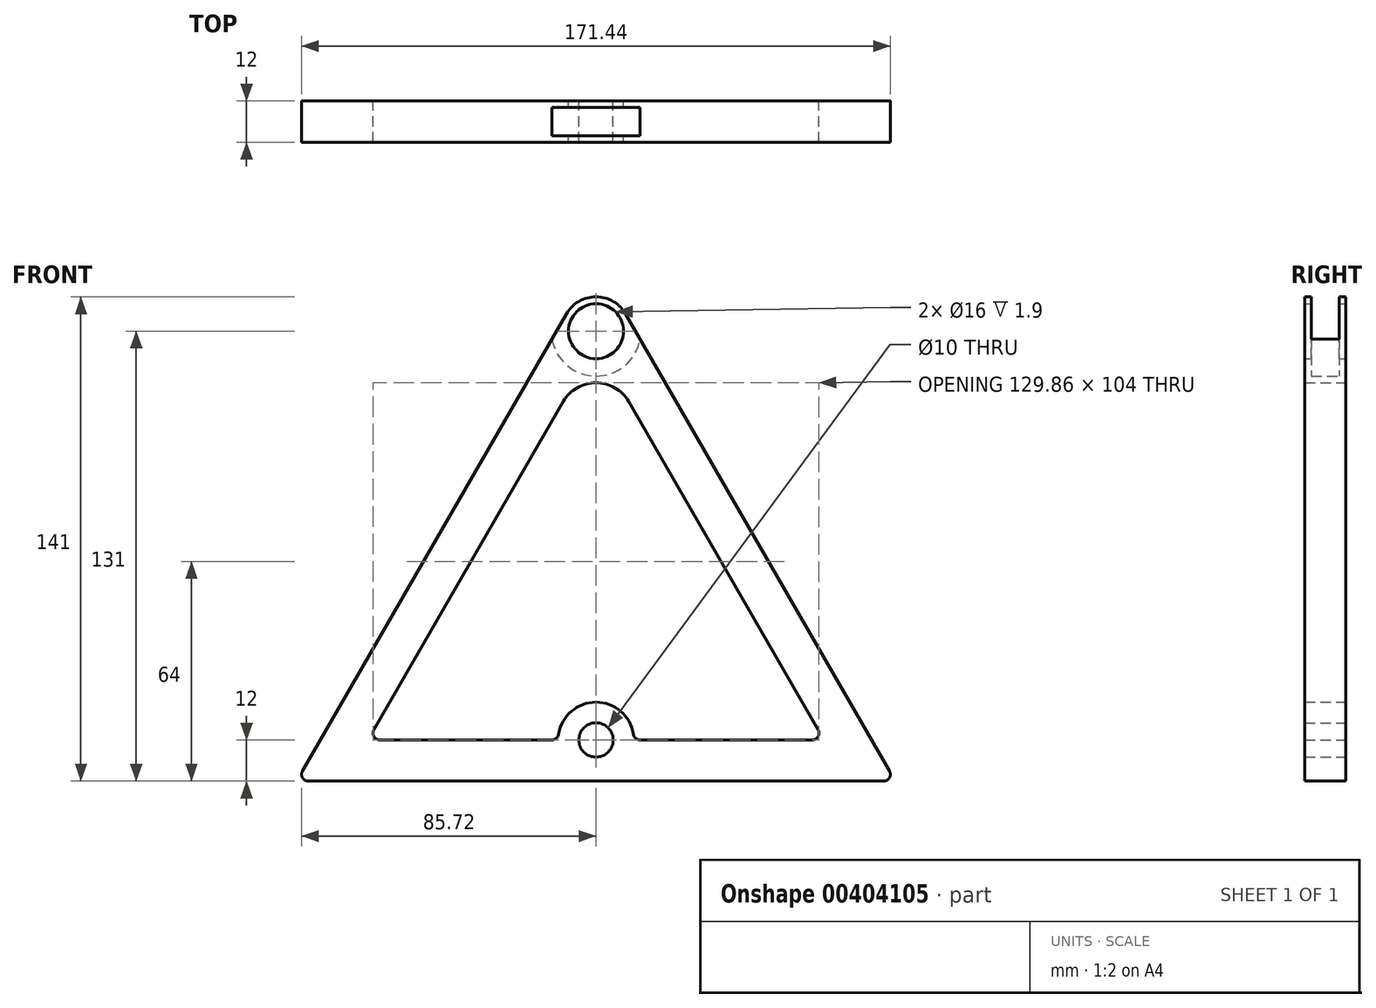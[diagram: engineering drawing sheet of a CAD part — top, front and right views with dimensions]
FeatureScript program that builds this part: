
annotation { "Feature Type Name" : "Feature", "Feature Type Description" : "" }
export const myFeature = defineFeature(function(context is Context, id is Id, definition is map)
    precondition{}
    {
        {
            var Q0;
            Q0=qCreatedBy(makeId("Front.planeOp"),FACE);
            var sketch = newSketch(context, id + "F0", { "sketchPlane" : qUnion([Q0])});
            skCircle(sketch, "E0", {"center": v(0, 125) * mm, "radius": 8 * mm, "construction": true});
            skCircle(sketch, "E1", {"center": v(0, 125) * mm, "radius": 5 * mm, "construction": true});
            skLineSegment(sketch, "E2", {"start": v(-72.17, 0) * mm, "end": v(72.17, 0) * mm, "construction": true});
            skLineSegment(sketch, "E3", {"start": v(72.17, 0) * mm, "end": v(0, 125) * mm, "construction": true});
            skLineSegment(sketch, "E4", {"start": v(0, 125) * mm, "end": v(-72.17, 0) * mm, "construction": true});
            skSolve(sketch);
        }
        {
            var Q0;
            Q0=qCreatedBy(makeId("Front.planeOp"),FACE);
            var sketch = newSketch(context, id + "F1", { "sketchPlane" : qUnion([Q0])});
            skLineSegment(sketch, "E5", {"start": v(-83.72, -6) * mm, "end": v(83.72, -6) * mm});
            skLineSegment(sketch, "E6", {"start": v(85.45, -3) * mm, "end": v(8.66, 130) * mm});
            skLineSegment(sketch, "E7", {"start": v(-85.45, -3) * mm, "end": v(-8.66, 130) * mm});
            skLineSegment(sketch, "E8", {"start": v(-62.93, 6) * mm, "end": v(-12.85, 6) * mm});
            skLineSegment(sketch, "E9", {"start": v(64.66, 9) * mm, "end": v(9.53, 104.5) * mm});
            skLineSegment(sketch, "E10", {"start": v(-64.66, 9) * mm, "end": v(-9.53, 104.5) * mm});
            skCircle(sketch, "E11", {"center": v(0, 6) * mm, "radius": 5 * mm});
            skArc(sketch, "E12", {"start": v(10.87, 7.7) * mm, "mid": v(0, 17) * mm, "end": v(-10.87, 7.7) * mm});
            skLineSegment(sketch, "E13.trimOffspring", {"start": v(12.85, 6) * mm, "end": v(62.93, 6) * mm});
            skPoint(sketch, "E14.visualSharp", {"position": v(-87.18, -6) * mm});
            skArc(sketch, "E14.filletArc", {"start": v(-85.45, -3) * mm, "mid": v(-85.45, -5) * mm, "end": v(-83.72, -6) * mm});
            skPoint(sketch, "E15.visualSharp", {"position": v(87.18, -6) * mm});
            skArc(sketch, "E15.filletArc", {"start": v(83.72, -6) * mm, "mid": v(85.45, -5) * mm, "end": v(85.45, -3) * mm});
            skPoint(sketch, "E16.visualSharp", {"position": v(66.4, 6) * mm});
            skArc(sketch, "E16.filletArc", {"start": v(62.93, 6) * mm, "mid": v(64.66, 7) * mm, "end": v(64.66, 9) * mm});
            skPoint(sketch, "E17.visualSharp", {"position": v(-66.4, 6) * mm});
            skArc(sketch, "E17.filletArc", {"start": v(-64.66, 9) * mm, "mid": v(-64.66, 7) * mm, "end": v(-62.93, 6) * mm});
            skPoint(sketch, "E18.visualSharp", {"position": v(-11, 6) * mm});
            skArc(sketch, "E18.filletArc", {"start": v(-12.85, 6) * mm, "mid": v(-11.54, 6.48) * mm, "end": v(-10.87, 7.7) * mm});
            skPoint(sketch, "E19.visualSharp", {"position": v(11, 6) * mm});
            skArc(sketch, "E19.filletArc", {"start": v(10.87, 7.7) * mm, "mid": v(11.54, 6.48) * mm, "end": v(12.85, 6) * mm});
            skArc(sketch, "E20", {"start": v(9.53, 104.5) * mm, "mid": v(0, 110) * mm, "end": v(-9.53, 104.5) * mm});
            skArc(sketch, "E21", {"start": v(8.66, 130) * mm, "mid": v(0, 135) * mm, "end": v(-8.66, 130) * mm});
            skCircle(sketch, "E22", {"center": v(0, 125) * mm, "radius": 8 * mm});
            skSolve(sketch);
        }
        {
            var Q0;
            Q0=qSketchRegion(id+"F1",true);
            extrude(context, id + "F2", {"entities" : qUnion([Q0]), "endBound" : BoundingType.SYMMETRIC, "depth" : 12 * mm});
        }
        {
            var Q0;
            Q0=qCreatedBy(makeId("Front.planeOp"),FACE);
            var sketch = newSketch(context, id + "F3", { "sketchPlane" : qUnion([Q0])});
            skCircle(sketch, "E23", {"center": v(0, 125) * mm, "radius": 13.05 * mm});
            skSolve(sketch);
        }
        {
            var Q0;
            Q0=qSketchRegion(id+"F3",true);
            var Q1;
            Q1=sQuery(id+"F3.wireOp",EDGE,"E23");
            extrude(context, id + "F4", {"entities" : qUnion([Q0]), "operationType" : NewBodyOperationType.REMOVE, "surfaceEntities" : qUnion([Q1]), "endBound" : BoundingType.SYMMETRIC, "depth" : 8.2 * mm});
        }
    });
